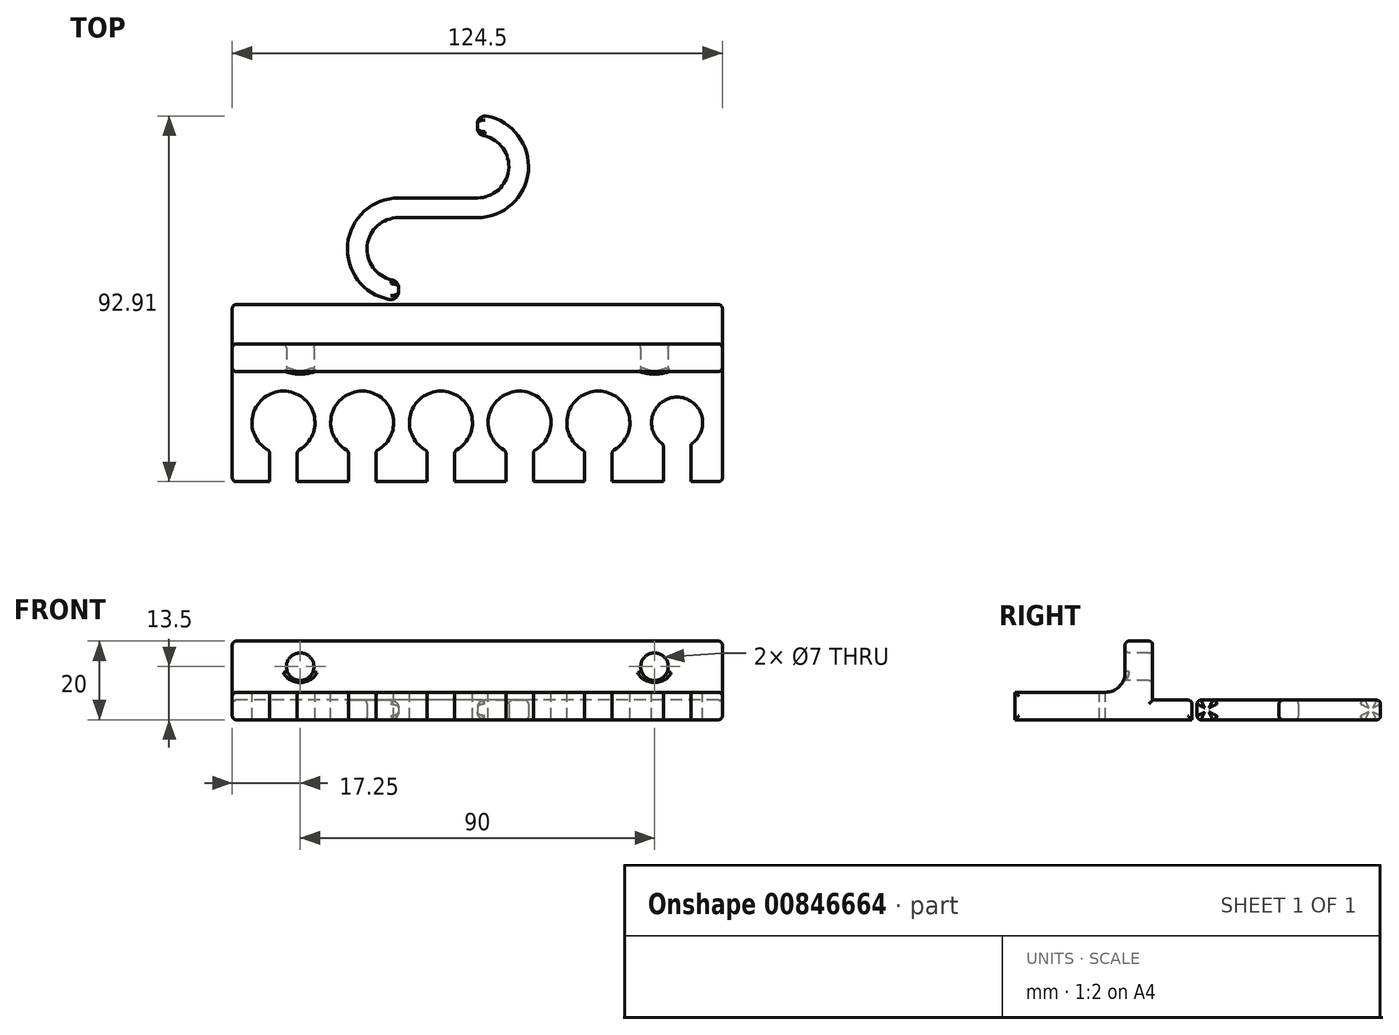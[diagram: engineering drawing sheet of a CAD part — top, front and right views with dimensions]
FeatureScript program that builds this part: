
annotation { "Feature Type Name" : "Feature", "Feature Type Description" : "" }
export const myFeature = defineFeature(function(context is Context, id is Id, definition is map)
    precondition{}
    {
        {
            var Q0;
            Q0=qCreatedBy(makeId("Front.planeOp"),FACE);
            var sketch = newSketch(context, id + "F0", { "sketchPlane" : qUnion([Q0])});
            skLineSegment(sketch, "E0.bottom", {"start": v(0, 0) * mm, "end": v(-62.25, 0) * mm});
            skLineSegment(sketch, "E0.top", {"start": v(0, 7) * mm, "end": v(-62.25, 7) * mm});
            skLineSegment(sketch, "E0.left", {"start": v(0, 0) * mm, "end": v(0, 7) * mm});
            skLineSegment(sketch, "E0.right", {"start": v(-62.25, 0) * mm, "end": v(-62.25, 7) * mm});
            skSolve(sketch);
        }
        {
            var Q0;
            Q0=makeQuery(id+"F0.imprint","IMPRINT",FACE,{"disambiguationData":[TD([[makeQuery(id+"F0.imprint","IMPRINT",EDGE,{"derivedFrom":sQuery(id+"F0.wireOp",EDGE,"E0.bottom")}),-1.0]])]});
            extrude(context, id + "F1", {"entities" : qUnion([Q0]), "depth" : 35 * mm, "offsetDistance" : 25 * mm});
        }
        {
            var Q0;
            Q0=makeQuery(id+"F1.opExtrude","SWEPT_FACE",FACE,{"disambiguationData":[OSD([sQuery(id+"F0.wireOp",EDGE,"E0.top")])]});
            var sketch = newSketch(context, id + "F2", { "sketchPlane" : qUnion([Q0])});
            skCircle(sketch, "E1", {"center": v(-49.25, -20) * mm, "radius": 8 * mm});
            skLineSegment(sketch, "E2", {"start": v(-52.75, -12.8) * mm, "end": v(-52.75, -35) * mm});
            skLineSegment(sketch, "E3", {"start": v(-49.25, -20) * mm, "end": v(-49.25, -35) * mm, "construction": true});
            skLineSegment(sketch, "E4.MirrorCS", {"start": v(-45.75, -12.8) * mm, "end": v(-45.75, -35) * mm});
            skCircle(sketch, "E5.1.0.0", {"center": v(-29.25, -20) * mm, "radius": 8 * mm});
            skLineSegment(sketch, "E5.1.0.1", {"start": v(-32.75, -12.8) * mm, "end": v(-32.75, -35) * mm});
            skLineSegment(sketch, "E5.1.0.2", {"start": v(-25.75, -12.8) * mm, "end": v(-25.75, -35) * mm});
            skLineSegment(sketch, "E5.1.0.3", {"start": v(-29.25, -20) * mm, "end": v(-29.25, -35) * mm, "construction": true});
            skCircle(sketch, "E5.2.0.0", {"center": v(-9.25, -20) * mm, "radius": 8 * mm});
            skLineSegment(sketch, "E5.2.0.1", {"start": v(-12.75, -12.8) * mm, "end": v(-12.75, -35) * mm});
            skLineSegment(sketch, "E5.2.0.2", {"start": v(-5.75, -12.8) * mm, "end": v(-5.75, -35) * mm});
            skLineSegment(sketch, "E5.2.0.3", {"start": v(-9.25, -20) * mm, "end": v(-9.25, -35) * mm, "construction": true});
            skCircle(sketch, "E5.3.0.0", {"center": v(10.75, -20) * mm, "radius": 8 * mm});
            skLineSegment(sketch, "E5.3.0.1", {"start": v(7.25, -12.8) * mm, "end": v(7.25, -35) * mm});
            skLineSegment(sketch, "E5.3.0.2", {"start": v(14.25, -12.8) * mm, "end": v(14.25, -35) * mm});
            skLineSegment(sketch, "E5.3.0.3", {"start": v(10.75, -20) * mm, "end": v(10.75, -35) * mm, "construction": true});
            skCircle(sketch, "E5.4.0.0", {"center": v(30.75, -20) * mm, "radius": 8 * mm});
            skLineSegment(sketch, "E5.4.0.1", {"start": v(27.25, -12.8) * mm, "end": v(27.25, -35) * mm});
            skLineSegment(sketch, "E5.4.0.2", {"start": v(34.25, -12.8) * mm, "end": v(34.25, -35) * mm});
            skLineSegment(sketch, "E5.4.0.3", {"start": v(30.75, -20) * mm, "end": v(30.75, -35) * mm, "construction": true});
            skLineSegment(sketch, "E5.direction1", {"start": v(-52.75, -35) * mm, "end": v(-32.75, -35) * mm, "construction": true});
            skCircle(sketch, "E6", {"center": v(50.75, -20) * mm, "radius": 6.5 * mm});
            skLineSegment(sketch, "E7", {"start": v(50.75, -20) * mm, "end": v(50.75, -35) * mm, "construction": true});
            skLineSegment(sketch, "E8", {"start": v(47.25, -14.52) * mm, "end": v(47.25, -35) * mm});
            skLineSegment(sketch, "E9.MirrorCS", {"start": v(54.25, -14.52) * mm, "end": v(54.25, -35) * mm});
            skLineSegment(sketch, "E10", {"start": v(7.25, -35) * mm, "end": v(14.25, -35) * mm});
            skLineSegment(sketch, "E11", {"start": v(27.25, -35) * mm, "end": v(34.25, -35) * mm});
            skLineSegment(sketch, "E12", {"start": v(47.25, -35) * mm, "end": v(54.25, -35) * mm});
            skSolve(sketch);
        }
        {
            var Q0;
            Q0=makeQuery(id+"F1.opExtrude","SWEPT_BODY",BODY,{"disambiguationData":[OSD([sQuery(id+"F0.wireOp",EDGE,"E0.bottom"),sQuery(id+"F0.wireOp",EDGE,"E0.top"),sQuery(id+"F0.wireOp",EDGE,"E0.left"),sQuery(id+"F0.wireOp",EDGE,"E0.right")])]});
            var Q1;
            Q1=qCreatedBy(makeId("Right.planeOp"),FACE);
            mirror(context, id + "F3", {"operationType" : NewBodyOperationType.ADD, "entities" : qUnion([Q0]), "mirrorPlane" : qUnion([Q1])});
        }
        {
            var Q0;
            Q0 = qSketchRegion(id + "F2", true);
            var Q1;
            {var subQ0=sQuery(id+"F2.wireOp",EDGE,"E2");var subQ1=sQuery(id+"F2.wireOp",EDGE,"E1");var subQ2=makeQuery(id+"F2.imprint","INTERSECT",VERTEX,{"disambiguationData":[OD(1.0)],"derivedFrom":[subQ1,subQ0]});Q1=makeQuery(id+"F2.imprint","IMPRINT",FACE,{"disambiguationData":[TD([[makeQuery(id+"F2.imprint","IMPRINT",EDGE,{"disambiguationData":[TD([[subQ2,-1.0]])],"derivedFrom":subQ1}),-1.0]])]});}
            var Q2;
            {var subQ0=sQuery(id+"F2.wireOp",EDGE,"E5.2.0.1");var subQ1=sQuery(id+"F2.wireOp",EDGE,"E5.2.0.0");var subQ2=makeQuery(id+"F2.imprint","INTERSECT",VERTEX,{"disambiguationData":[OD(1.0)],"derivedFrom":[subQ1,subQ0]});Q2=makeQuery(id+"F2.imprint","IMPRINT",FACE,{"disambiguationData":[TD([[makeQuery(id+"F2.imprint","IMPRINT",EDGE,{"disambiguationData":[TD([[subQ2,-1.0]])],"derivedFrom":subQ1}),-1.0]])]});}
            var Q3;
            {var subQ0=sQuery(id+"F2.wireOp",EDGE,"E5.1.0.1");var subQ1=sQuery(id+"F2.wireOp",EDGE,"E5.1.0.0");var subQ2=makeQuery(id+"F2.imprint","INTERSECT",VERTEX,{"disambiguationData":[OD(1.0)],"derivedFrom":[subQ1,subQ0]});Q3=makeQuery(id+"F2.imprint","IMPRINT",FACE,{"disambiguationData":[TD([[makeQuery(id+"F2.imprint","IMPRINT",EDGE,{"disambiguationData":[TD([[subQ2,-1.0]])],"derivedFrom":subQ1}),-1.0]])]});}
            extrude(context, id + "F4", {"entities" : qUnion([Q0, Q1, Q2, Q3]), "operationType" : NewBodyOperationType.REMOVE, "oppositeDirection" : true, "depth" : 25 * mm, "offsetDistance" : 25 * mm});
        }
        {
            var Q0;
            Q0=makeQuery(id+"F1.opExtrude","SWEPT_FACE",FACE,{"disambiguationData":[OSD([sQuery(id+"F0.wireOp",EDGE,"E0.right")])]});
            var sketch = newSketch(context, id + "F5", { "sketchPlane" : qUnion([Q0])});
            skLineSegment(sketch, "E13.bottom", {"start": v(0, 0) * mm, "end": v(7, 0) * mm});
            skLineSegment(sketch, "E13.top", {"start": v(0, 20) * mm, "end": v(7, 20) * mm});
            skLineSegment(sketch, "E13.left", {"start": v(0, 0) * mm, "end": v(0, 20) * mm});
            skLineSegment(sketch, "E13.right", {"start": v(7, 0) * mm, "end": v(7, 20) * mm});
            skSolve(sketch);
        }
        {
            var Q0;
            Q0 = qSketchRegion(id + "F5", true);
            var Q1;
            Q1=makeQuery(id+"F3.opPattern","COPY",FACE,{"derivedFrom":makeQuery(id+"F1.opExtrude","SWEPT_FACE",FACE,{"disambiguationData":[OSD([sQuery(id+"F0.wireOp",EDGE,"E0.right")])]}),"instanceName":"1"});
            extrude(context, id + "F6", {"entities" : qUnion([Q0]), "operationType" : NewBodyOperationType.ADD, "endBound" : BoundingType.UP_TO_SURFACE, "oppositeDirection" : true, "depth" : 25 * mm, "endBoundEntityFace" : qUnion([Q1]), "offsetDistance" : 25 * mm});
        }
        {
            var Q0;
            {var subQ0=makeQuery(id+"F1.opExtrude","CAP_FACE",FACE,{"disambiguationData":[OSD([sQuery(id+"F0.wireOp",EDGE,"E0.bottom"),sQuery(id+"F0.wireOp",EDGE,"E0.top"),sQuery(id+"F0.wireOp",EDGE,"E0.left"),sQuery(id+"F0.wireOp",EDGE,"E0.right")])],"isStart":true});Q0=makeQuery(id+"F6.boolean.opBoolean","MERGE",FACE,{"derivedFrom":[makeQuery(id+"F3.boolean.opBoolean","MERGE",FACE,{"derivedFrom":[subQ0,makeQuery(id+"F3.opPattern","COPY",FACE,{"derivedFrom":subQ0,"instanceName":"1"})]}),makeQuery(id+"F6.opExtrude","SWEPT_FACE",FACE,{"disambiguationData":[OSD([sQuery(id+"F5.wireOp",EDGE,"E13.left")])]})]});}
            var sketch = newSketch(context, id + "F7", { "sketchPlane" : qUnion([Q0])});
            skLineSegment(sketch, "E14.bottom", {"start": v(-62.25, 0) * mm, "end": v(62.25, 0) * mm});
            skLineSegment(sketch, "E14.top", {"start": v(-62.25, 5) * mm, "end": v(62.25, 5) * mm});
            skLineSegment(sketch, "E14.left", {"start": v(-62.25, 0) * mm, "end": v(-62.25, 5) * mm});
            skLineSegment(sketch, "E14.right", {"start": v(62.25, 0) * mm, "end": v(62.25, 5) * mm});
            skSolve(sketch);
        }
        {
            var Q0;
            Q0=makeQuery(id+"F7.imprint","IMPRINT",FACE,{"disambiguationData":[TD([[makeQuery(id+"F7.imprint","IMPRINT",EDGE,{"derivedFrom":sQuery(id+"F7.wireOp",EDGE,"E14.bottom")}),1.0]])]});
            extrude(context, id + "F8", {"entities" : qUnion([Q0]), "operationType" : NewBodyOperationType.ADD, "depth" : 10 * mm, "offsetDistance" : 25 * mm});
        }
        {
            var Q0;
            {var subQ0=makeQuery(id+"F1.opExtrude","SWEPT_FACE",FACE,{"disambiguationData":[OSD([sQuery(id+"F0.wireOp",EDGE,"E0.top")])]});Q0=makeQuery(id+"F6.boolean.opBoolean","INTERSECT",EDGE,{"derivedFrom":[makeQuery(id+"F3.boolean.opBoolean","MERGE",FACE,{"derivedFrom":[subQ0,makeQuery(id+"F3.opPattern","COPY",FACE,{"derivedFrom":subQ0,"instanceName":"1"})]}),makeQuery(id+"F6.opExtrude","SWEPT_FACE",FACE,{"disambiguationData":[OSD([sQuery(id+"F5.wireOp",EDGE,"E13.right")])]})]});}
            var Q1;
            Q1=makeQuery(id+"F8.opExtrude","CAP_EDGE",EDGE,{"disambiguationData":[OSD([sQuery(id+"F7.wireOp",EDGE,"E14.top")])],"isStart":true});
            fillet(context, id + "F9", {"entities" : qUnion([Q0, Q1]), "radius" : 5 * mm, "tangentPropagation" : true, "allowEdgeOverflow" : false});
        }
        {
            var Q0;
            Q0=makeQuery(id+"F6.opExtrude","SWEPT_FACE",FACE,{"disambiguationData":[OSD([sQuery(id+"F5.wireOp",EDGE,"E13.right")])]});
            var sketch = newSketch(context, id + "F10", { "sketchPlane" : qUnion([Q0])});
            skCircle(sketch, "E15", {"center": v(-45, 13.5) * mm, "radius": 3.5 * mm});
            skLineSegment(sketch, "E16", {"start": v(-62.25, 13.5) * mm, "end": v(62.25, 13.5) * mm, "construction": true});
            skLineSegment(sketch, "E17", {"start": v(-62.25, 20) * mm, "end": v(-62.25, 7) * mm});
            skLineSegment(sketch, "E18.0", {"start": v(-62.25, 0) * mm, "end": v(-62.25, 7) * mm});
            skPoint(sketch, "E19", {"position": v(-62.25, 13.5) * mm});
            skCircle(sketch, "E20.MirrorC", {"center": v(45, 13.5) * mm, "radius": 3.5 * mm});
            skSolve(sketch);
        }
        {
            var Q0;
            Q0 = qSketchRegion(id + "F10", true);
            extrude(context, id + "F11", {"entities" : qUnion([Q0]), "operationType" : NewBodyOperationType.REMOVE, "endBound" : BoundingType.THROUGH_ALL, "oppositeDirection" : true, "depth" : 25 * mm, "offsetDistance" : 25 * mm, "hasSecondDirection" : true, "secondDirectionBound" : BoundingType.THROUGH_ALL, "secondDirectionOppositeDirection" : false, "secondDirectionDepth" : 25 * mm});
        }
        {
            var Q0;
            Q0=makeQuery(id+"F4.boolean.opBoolean","COPY",EDGE,{"derivedFrom":makeQuery(id+"F4.opExtrude","CAP_EDGE",EDGE,{"disambiguationData":[OSD([sQuery(id+"F2.wireOp",EDGE,"E1")])],"isStart":true})});
            var Q1;
            Q1=makeQuery(id+"F4.boolean.opBoolean","COPY",EDGE,{"derivedFrom":makeQuery(id+"F4.opExtrude","CAP_EDGE",EDGE,{"disambiguationData":[OSD([sQuery(id+"F2.wireOp",EDGE,"E5.1.0.0")])],"isStart":true})});
            var Q2;
            Q2=makeQuery(id+"F4.boolean.opBoolean","COPY",EDGE,{"derivedFrom":makeQuery(id+"F4.opExtrude","CAP_EDGE",EDGE,{"disambiguationData":[OSD([sQuery(id+"F2.wireOp",EDGE,"E5.2.0.0")])],"isStart":true})});
            var Q3;
            Q3=makeQuery(id+"F4.boolean.opBoolean","COPY",EDGE,{"derivedFrom":makeQuery(id+"F4.opExtrude","CAP_EDGE",EDGE,{"disambiguationData":[OSD([sQuery(id+"F2.wireOp",EDGE,"E5.3.0.0")])],"isStart":true})});
            var Q4;
            Q4=makeQuery(id+"F4.boolean.opBoolean","COPY",EDGE,{"derivedFrom":makeQuery(id+"F4.opExtrude","CAP_EDGE",EDGE,{"disambiguationData":[OSD([sQuery(id+"F2.wireOp",EDGE,"E5.4.0.0")])],"isStart":true})});
            var Q5;
            Q5=makeQuery(id+"F4.boolean.opBoolean","COPY",EDGE,{"derivedFrom":makeQuery(id+"F4.opExtrude","CAP_EDGE",EDGE,{"disambiguationData":[OSD([sQuery(id+"F2.wireOp",EDGE,"E6")])],"isStart":true})});
            var Q6;
            Q6=makeQuery(id+"F11.boolean.opBoolean","INTERSECT",EDGE,{"derivedFrom":[makeQuery(id+"F6.opExtrude","SWEPT_FACE",FACE,{"disambiguationData":[OSD([sQuery(id+"F5.wireOp",EDGE,"E13.right")])]}),makeQuery(id+"F11.opExtrude","SWEPT_FACE",FACE,{"disambiguationData":[OSD([sQuery(id+"F10.wireOp",EDGE,"E15")])]})]});
            var Q7;
            Q7=makeQuery(id+"F11.boolean.opBoolean","INTERSECT",EDGE,{"derivedFrom":[makeQuery(id+"F6.opExtrude","SWEPT_FACE",FACE,{"disambiguationData":[OSD([sQuery(id+"F5.wireOp",EDGE,"E13.right")])]}),makeQuery(id+"F11.opExtrude","SWEPT_FACE",FACE,{"disambiguationData":[OSD([sQuery(id+"F10.wireOp",EDGE,"E20.MirrorC")])]})]});
            var Q8;
            {var subQ0=makeQuery(id+"F1.opExtrude","CAP_FACE",FACE,{"disambiguationData":[OSD([sQuery(id+"F0.wireOp",EDGE,"E0.bottom"),sQuery(id+"F0.wireOp",EDGE,"E0.top"),sQuery(id+"F0.wireOp",EDGE,"E0.left"),sQuery(id+"F0.wireOp",EDGE,"E0.right")])],"isStart":true});Q8=makeQuery(id+"F11.boolean.opBoolean","INTERSECT",EDGE,{"derivedFrom":[makeQuery(id+"F6.boolean.opBoolean","MERGE",FACE,{"derivedFrom":[makeQuery(id+"F3.boolean.opBoolean","MERGE",FACE,{"derivedFrom":[subQ0,makeQuery(id+"F3.opPattern","COPY",FACE,{"derivedFrom":subQ0,"instanceName":"1"})]}),makeQuery(id+"F6.opExtrude","SWEPT_FACE",FACE,{"disambiguationData":[OSD([sQuery(id+"F5.wireOp",EDGE,"E13.left")])]})]}),makeQuery(id+"F11.opExtrude","SWEPT_FACE",FACE,{"disambiguationData":[OSD([sQuery(id+"F10.wireOp",EDGE,"E15")])]})]});}
            var Q9;
            {var subQ0=makeQuery(id+"F1.opExtrude","CAP_FACE",FACE,{"disambiguationData":[OSD([sQuery(id+"F0.wireOp",EDGE,"E0.bottom"),sQuery(id+"F0.wireOp",EDGE,"E0.top"),sQuery(id+"F0.wireOp",EDGE,"E0.left"),sQuery(id+"F0.wireOp",EDGE,"E0.right")])],"isStart":true});Q9=makeQuery(id+"F11.boolean.opBoolean","INTERSECT",EDGE,{"derivedFrom":[makeQuery(id+"F6.boolean.opBoolean","MERGE",FACE,{"derivedFrom":[makeQuery(id+"F3.boolean.opBoolean","MERGE",FACE,{"derivedFrom":[subQ0,makeQuery(id+"F3.opPattern","COPY",FACE,{"derivedFrom":subQ0,"instanceName":"1"})]}),makeQuery(id+"F6.opExtrude","SWEPT_FACE",FACE,{"disambiguationData":[OSD([sQuery(id+"F5.wireOp",EDGE,"E13.left")])]})]}),makeQuery(id+"F11.opExtrude","SWEPT_FACE",FACE,{"disambiguationData":[OSD([sQuery(id+"F10.wireOp",EDGE,"E20.MirrorC")])]})]});}
            var Q10;
            Q10=makeQuery(id+"F6.boolean.opBoolean","MERGE",FACE,{"derivedFrom":[makeQuery(id+"F1.opExtrude","SWEPT_FACE",FACE,{"disambiguationData":[OSD([sQuery(id+"F0.wireOp",EDGE,"E0.right")])]}),makeQuery(id+"F6.opExtrude","CAP_FACE",FACE,{"disambiguationData":[OSD([sQuery(id+"F5.wireOp",EDGE,"E13.bottom"),sQuery(id+"F5.wireOp",EDGE,"E13.top"),sQuery(id+"F5.wireOp",EDGE,"E13.left"),sQuery(id+"F5.wireOp",EDGE,"E13.right")])],"isStart":true})]});
            var Q11;
            {var subQ0=sQuery(id+"F0.wireOp",EDGE,"E0.right");Q11=makeQuery(id+"F6.boolean.opBoolean","MERGE",FACE,{"derivedFrom":[makeQuery(id+"F3.opPattern","COPY",FACE,{"derivedFrom":makeQuery(id+"F1.opExtrude","SWEPT_FACE",FACE,{"disambiguationData":[OSD([subQ0])]}),"instanceName":"1"}),makeQuery(id+"F6.opExtrude","CAP_FACE",FACE,{"disambiguationData":[OSD([subQ0])],"isStart":false})]});}
            var Q12;
            Q12=makeQuery(id+"F4.boolean.opBoolean","COPY",EDGE,{"derivedFrom":makeQuery(id+"F4.opExtrude","SWEPT_EDGE",EDGE,{"disambiguationData":[OSD([sQuery(id+"F0.wireOp",EDGE,"E0.top"),sQuery(id+"F2.wireOp",EDGE,"E2")])]})});
            var Q13;
            Q13=makeQuery(id+"F4.boolean.opBoolean","COPY",EDGE,{"derivedFrom":makeQuery(id+"F4.opExtrude","SWEPT_EDGE",EDGE,{"disambiguationData":[OSD([sQuery(id+"F2.wireOp",EDGE,"E1"),sQuery(id+"F2.wireOp",EDGE,"E2")])]})});
            var Q14;
            Q14=makeQuery(id+"F4.boolean.opBoolean","COPY",EDGE,{"derivedFrom":makeQuery(id+"F4.opExtrude","SWEPT_EDGE",EDGE,{"disambiguationData":[OSD([sQuery(id+"F0.wireOp",EDGE,"E0.top"),sQuery(id+"F2.wireOp",EDGE,"E4.MirrorCS")])]})});
            var Q15;
            Q15=makeQuery(id+"F4.boolean.opBoolean","COPY",EDGE,{"derivedFrom":makeQuery(id+"F4.opExtrude","SWEPT_EDGE",EDGE,{"disambiguationData":[OSD([sQuery(id+"F0.wireOp",EDGE,"E0.top"),sQuery(id+"F2.wireOp",EDGE,"E5.1.0.1")])]})});
            var Q16;
            Q16=makeQuery(id+"F4.boolean.opBoolean","COPY",EDGE,{"derivedFrom":makeQuery(id+"F4.opExtrude","SWEPT_EDGE",EDGE,{"disambiguationData":[OSD([sQuery(id+"F0.wireOp",EDGE,"E0.top"),sQuery(id+"F2.wireOp",EDGE,"E5.1.0.2")])]})});
            var Q17;
            Q17=makeQuery(id+"F4.boolean.opBoolean","COPY",EDGE,{"derivedFrom":makeQuery(id+"F4.opExtrude","SWEPT_EDGE",EDGE,{"disambiguationData":[OSD([sQuery(id+"F0.wireOp",EDGE,"E0.top"),sQuery(id+"F2.wireOp",EDGE,"E5.2.0.1")])]})});
            var Q18;
            Q18=makeQuery(id+"F4.boolean.opBoolean","COPY",EDGE,{"derivedFrom":makeQuery(id+"F4.opExtrude","SWEPT_EDGE",EDGE,{"disambiguationData":[OSD([sQuery(id+"F0.wireOp",EDGE,"E0.top"),sQuery(id+"F2.wireOp",EDGE,"E5.2.0.2")])]})});
            var Q19;
            Q19=makeQuery(id+"F4.boolean.opBoolean","COPY",EDGE,{"derivedFrom":makeQuery(id+"F4.opExtrude","SWEPT_EDGE",EDGE,{"disambiguationData":[OSD([sQuery(id+"F2.wireOp",EDGE,"E5.3.0.1"),sQuery(id+"F2.wireOp",EDGE,"E10")])]})});
            var Q20;
            Q20=makeQuery(id+"F4.boolean.opBoolean","COPY",EDGE,{"derivedFrom":makeQuery(id+"F4.opExtrude","SWEPT_EDGE",EDGE,{"disambiguationData":[OSD([sQuery(id+"F2.wireOp",EDGE,"E5.3.0.2"),sQuery(id+"F2.wireOp",EDGE,"E10")])]})});
            var Q21;
            Q21=makeQuery(id+"F4.boolean.opBoolean","COPY",EDGE,{"derivedFrom":makeQuery(id+"F4.opExtrude","SWEPT_EDGE",EDGE,{"disambiguationData":[OSD([sQuery(id+"F2.wireOp",EDGE,"E5.4.0.1"),sQuery(id+"F2.wireOp",EDGE,"E11")])]})});
            var Q22;
            Q22=makeQuery(id+"F4.boolean.opBoolean","COPY",EDGE,{"derivedFrom":makeQuery(id+"F4.opExtrude","SWEPT_EDGE",EDGE,{"disambiguationData":[OSD([sQuery(id+"F2.wireOp",EDGE,"E5.4.0.2"),sQuery(id+"F2.wireOp",EDGE,"E11")])]})});
            var Q23;
            Q23=makeQuery(id+"F4.boolean.opBoolean","COPY",EDGE,{"derivedFrom":makeQuery(id+"F4.opExtrude","SWEPT_EDGE",EDGE,{"disambiguationData":[OSD([sQuery(id+"F2.wireOp",EDGE,"E8"),sQuery(id+"F2.wireOp",EDGE,"E12")])]})});
            var Q24;
            Q24=makeQuery(id+"F4.boolean.opBoolean","COPY",EDGE,{"derivedFrom":makeQuery(id+"F4.opExtrude","SWEPT_EDGE",EDGE,{"disambiguationData":[OSD([sQuery(id+"F2.wireOp",EDGE,"E9.MirrorCS"),sQuery(id+"F2.wireOp",EDGE,"E12")])]})});
            var Q25;
            Q25=makeQuery(id+"F4.boolean.opBoolean","COPY",EDGE,{"derivedFrom":makeQuery(id+"F4.opExtrude","SWEPT_EDGE",EDGE,{"disambiguationData":[OSD([sQuery(id+"F2.wireOp",EDGE,"E6"),sQuery(id+"F2.wireOp",EDGE,"E8")])]})});
            var Q26;
            Q26=makeQuery(id+"F4.boolean.opBoolean","COPY",EDGE,{"derivedFrom":makeQuery(id+"F4.opExtrude","SWEPT_EDGE",EDGE,{"disambiguationData":[OSD([sQuery(id+"F2.wireOp",EDGE,"E5.4.0.0"),sQuery(id+"F2.wireOp",EDGE,"E5.4.0.1")])]})});
            var Q27;
            Q27=makeQuery(id+"F4.boolean.opBoolean","COPY",EDGE,{"derivedFrom":makeQuery(id+"F4.opExtrude","SWEPT_EDGE",EDGE,{"disambiguationData":[OSD([sQuery(id+"F2.wireOp",EDGE,"E5.3.0.0"),sQuery(id+"F2.wireOp",EDGE,"E5.3.0.1")])]})});
            var Q28;
            Q28=makeQuery(id+"F4.boolean.opBoolean","COPY",EDGE,{"derivedFrom":makeQuery(id+"F4.opExtrude","SWEPT_EDGE",EDGE,{"disambiguationData":[OSD([sQuery(id+"F2.wireOp",EDGE,"E5.2.0.0"),sQuery(id+"F2.wireOp",EDGE,"E5.2.0.1")])]})});
            var Q29;
            Q29=makeQuery(id+"F4.boolean.opBoolean","COPY",EDGE,{"derivedFrom":makeQuery(id+"F4.opExtrude","SWEPT_EDGE",EDGE,{"disambiguationData":[OSD([sQuery(id+"F2.wireOp",EDGE,"E5.1.0.0"),sQuery(id+"F2.wireOp",EDGE,"E5.1.0.1")])]})});
            var Q30;
            Q30=makeQuery(id+"F4.boolean.opBoolean","COPY",EDGE,{"derivedFrom":makeQuery(id+"F4.opExtrude","SWEPT_EDGE",EDGE,{"disambiguationData":[OSD([sQuery(id+"F2.wireOp",EDGE,"E6"),sQuery(id+"F2.wireOp",EDGE,"E9.MirrorCS")])]})});
            var Q31;
            Q31=makeQuery(id+"F4.boolean.opBoolean","COPY",EDGE,{"derivedFrom":makeQuery(id+"F4.opExtrude","SWEPT_EDGE",EDGE,{"disambiguationData":[OSD([sQuery(id+"F2.wireOp",EDGE,"E5.4.0.0"),sQuery(id+"F2.wireOp",EDGE,"E5.4.0.2")])]})});
            var Q32;
            Q32=makeQuery(id+"F4.boolean.opBoolean","COPY",EDGE,{"derivedFrom":makeQuery(id+"F4.opExtrude","SWEPT_EDGE",EDGE,{"disambiguationData":[OSD([sQuery(id+"F2.wireOp",EDGE,"E5.3.0.0"),sQuery(id+"F2.wireOp",EDGE,"E5.3.0.2")])]})});
            var Q33;
            Q33=makeQuery(id+"F4.boolean.opBoolean","COPY",EDGE,{"derivedFrom":makeQuery(id+"F4.opExtrude","SWEPT_EDGE",EDGE,{"disambiguationData":[OSD([sQuery(id+"F2.wireOp",EDGE,"E5.2.0.0"),sQuery(id+"F2.wireOp",EDGE,"E5.2.0.2")])]})});
            var Q34;
            Q34=makeQuery(id+"F4.boolean.opBoolean","COPY",EDGE,{"derivedFrom":makeQuery(id+"F4.opExtrude","SWEPT_EDGE",EDGE,{"disambiguationData":[OSD([sQuery(id+"F2.wireOp",EDGE,"E5.1.0.0"),sQuery(id+"F2.wireOp",EDGE,"E5.1.0.2")])]})});
            var Q35;
            Q35=makeQuery(id+"F4.boolean.opBoolean","COPY",EDGE,{"derivedFrom":makeQuery(id+"F4.opExtrude","SWEPT_EDGE",EDGE,{"disambiguationData":[OSD([sQuery(id+"F2.wireOp",EDGE,"E1"),sQuery(id+"F2.wireOp",EDGE,"E4.MirrorCS")])]})});
            var Q36;
            Q36=makeQuery(id+"F6.opExtrude","SWEPT_EDGE",EDGE,{"disambiguationData":[OSD([sQuery(id+"F5.wireOp",EDGE,"E13.top"),sQuery(id+"F5.wireOp",EDGE,"E13.right")])]});
            var Q37;
            Q37=makeQuery(id+"F6.opExtrude","SWEPT_EDGE",EDGE,{"disambiguationData":[OSD([sQuery(id+"F5.wireOp",EDGE,"E13.top"),sQuery(id+"F5.wireOp",EDGE,"E13.left")])]});
            var Q38;
            Q38=makeQuery(id+"F8.opExtrude","CAP_EDGE",EDGE,{"disambiguationData":[OSD([sQuery(id+"F7.wireOp",EDGE,"E14.top")])],"isStart":false});
            fillet(context, id + "F12", {"entities" : qUnion([Q0, Q1, Q2, Q3, Q4, Q5, Q6, Q7, Q8, Q9, Q10, Q11, Q12, Q13, Q14, Q15, Q16, Q17, Q18, Q19, Q20, Q21, Q22, Q23, Q24, Q25, Q26, Q27, Q28, Q29, Q30, Q31, Q32, Q33, Q34, Q35, Q36, Q37, Q38]), "radius" : 1 * mm, "tangentPropagation" : true, "allowEdgeOverflow" : false});
        }
        {
            var Q0;
            Q0=qCreatedBy(makeId("Top.planeOp"),FACE);
            var sketch = newSketch(context, id + "F13", { "sketchPlane" : qUnion([Q0])});
            skPoint(sketch, "E21", {"position": v(-20, 24.1) * mm});
            skLineSegment(sketch, "E22", {"start": v(0, 45.1) * mm, "end": v(0, 0) * mm, "construction": true});
            skLineSegment(sketch, "E23", {"start": v(0, 37.1) * mm, "end": v(-20, 37.1) * mm});
            skArc(sketch, "E24", {"start": v(-20, 37.1) * mm, "mid": v(-33, 24.1) * mm, "end": v(-20, 11.1) * mm});
            skArc(sketch, "E25", {"start": v(0, 37.1) * mm, "mid": v(8, 45.1) * mm, "end": v(0, 53.1) * mm});
            skArc(sketch, "E26.0", {"start": v(0, 32.1) * mm, "mid": v(13, 45.1) * mm, "end": v(0, 58.1) * mm});
            skLineSegment(sketch, "E26.1", {"start": v(0, 32.1) * mm, "end": v(-20, 32.1) * mm});
            skArc(sketch, "E26.2", {"start": v(-20, 32.1) * mm, "mid": v(-28, 24.1) * mm, "end": v(-20, 16.1) * mm});
            skLineSegment(sketch, "E27", {"start": v(-20, 16.1) * mm, "end": v(-20, 11.1) * mm});
            skLineSegment(sketch, "E28", {"start": v(0, 58.1) * mm, "end": v(0, 53.1) * mm});
            skSolve(sketch);
        }
        {
            var Q0;
            Q0=makeQuery(id+"F13.imprint","IMPRINT",FACE,{"disambiguationData":[TD([[makeQuery(id+"F13.imprint","IMPRINT",EDGE,{"derivedFrom":sQuery(id+"F13.wireOp",EDGE,"E23")}),1.0]])]});
            extrude(context, id + "F14", {"entities" : qUnion([Q0]), "depth" : 5 * mm, "offsetDistance" : 25 * mm});
        }
        {
            var Q0;
            Q0=makeQuery(id+"F14.opExtrude","SWEPT_FACE",FACE,{"disambiguationData":[OSD([sQuery(id+"F13.wireOp",EDGE,"E28")])]});
            var Q1;
            Q1=makeQuery(id+"F14.opExtrude","SWEPT_FACE",FACE,{"disambiguationData":[OSD([sQuery(id+"F13.wireOp",EDGE,"E27")])]});
            fillet(context, id + "F15", {"entities" : qUnion([Q0, Q1]), "radius" : 2 * mm, "tangentPropagation" : true, "allowEdgeOverflow" : false});
        }
        {
            var Q0;
            Q0=makeQuery(id+"F14.opExtrude","CAP_FACE",FACE,{"disambiguationData":[OSD([sQuery(id+"F13.wireOp",EDGE,"E23"),sQuery(id+"F13.wireOp",EDGE,"E24"),sQuery(id+"F13.wireOp",EDGE,"E25"),sQuery(id+"F13.wireOp",EDGE,"E26.0"),sQuery(id+"F13.wireOp",EDGE,"E26.1"),sQuery(id+"F13.wireOp",EDGE,"E26.2"),sQuery(id+"F13.wireOp",EDGE,"E27"),sQuery(id+"F13.wireOp",EDGE,"E28")])],"isStart":false});
            var Q1;
            Q1=makeQuery(id+"F14.opExtrude","CAP_FACE",FACE,{"disambiguationData":[OSD([sQuery(id+"F13.wireOp",EDGE,"E23"),sQuery(id+"F13.wireOp",EDGE,"E24"),sQuery(id+"F13.wireOp",EDGE,"E25"),sQuery(id+"F13.wireOp",EDGE,"E26.0"),sQuery(id+"F13.wireOp",EDGE,"E26.1"),sQuery(id+"F13.wireOp",EDGE,"E26.2"),sQuery(id+"F13.wireOp",EDGE,"E27"),sQuery(id+"F13.wireOp",EDGE,"E28")])],"isStart":true});
            fillet(context, id + "F16", {"entities" : qUnion([Q0, Q1]), "radius" : 1 * mm, "tangentPropagation" : true, "allowEdgeOverflow" : false});
        }
    });
